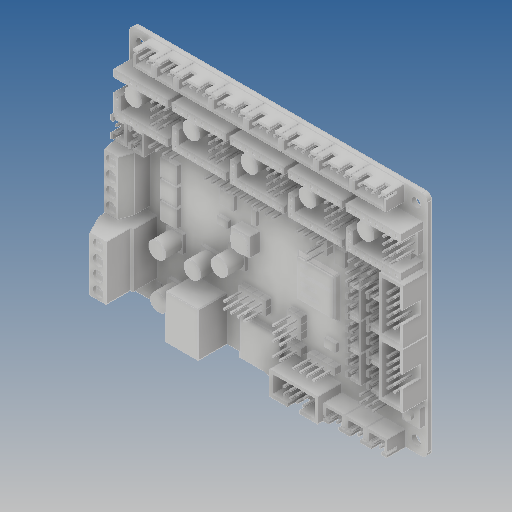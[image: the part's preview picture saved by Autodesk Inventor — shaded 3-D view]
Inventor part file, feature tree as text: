
AUTODESK INVENTOR PART (.ipt)
format: ipt  version: 2018 (Build 220112000, 112)  size: 3,010,048 bytes
history: native  units: mm
features: fillet x1
ambient origin geometry x8: Origin, YZ Plane, XZ Plane, XY Plane, X Axis, Y Axis, Z Axis, Center Point
bodies: Solid1 (feature_tree)
feature tree (1):
  fillet  "Fillet10"  [1 undecoded]
note: 1 required parameter value undecoded (feature->parameter linkage not recoverable at this tier; creation-order binding heuristic only, values carry confidence <= 0.55)
